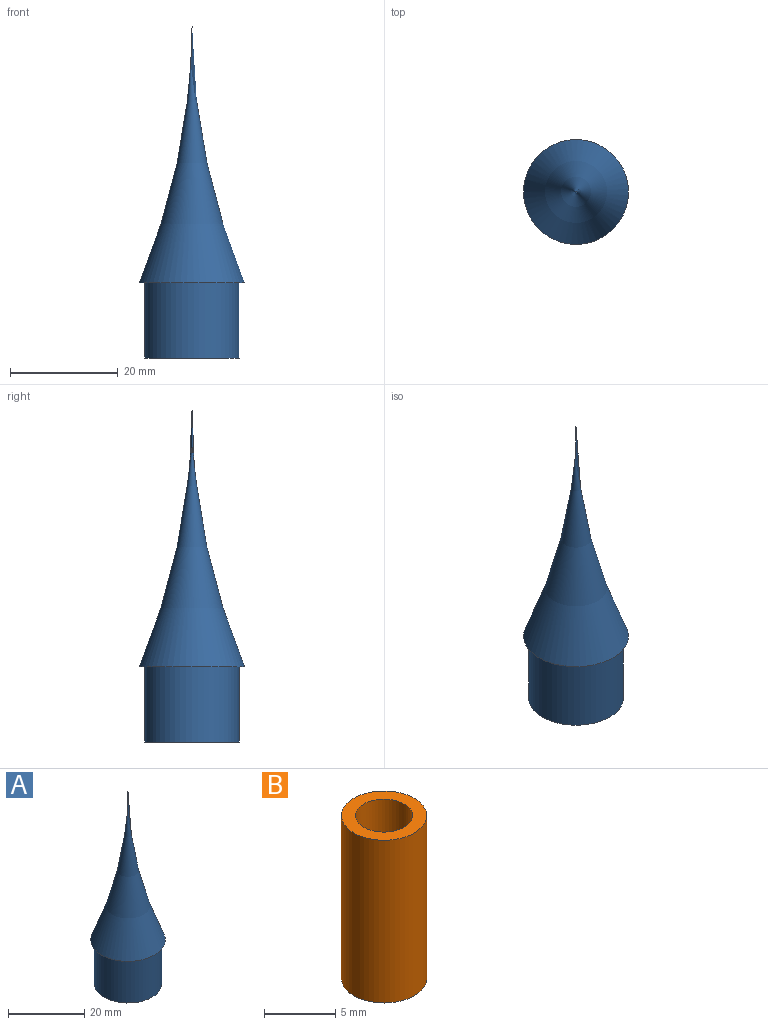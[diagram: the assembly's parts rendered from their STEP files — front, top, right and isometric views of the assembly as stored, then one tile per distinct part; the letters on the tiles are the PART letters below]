
ASSEMBLY  parts=2 mates=1
PART A: 7 faces, bbox 19.5x19.5x61.7 mm
  f0: plane 16.5x16.5mm, normal (0,0,1), area 22.7mm2, adj f1,f6
  f1: cylinder r=7.8mm len=15.6mm, axis (0,0,-1), area 735.1mm2, adj f0,f2
  f2: plane 17.6x17.6mm, normal (0,0,-1), area 52.2mm2, adj f1,f3
  f3: cylinder r=8.8mm len=17.6mm, axis (0,0,-1), area 774.1mm2, adj f2,f4
  f4: plane 19.49x19.49mm, normal (0,0,-1), area 55mm2, adj f3,f5
  f5: torus R=125.24mm, axis (0,0,-1), area 1019.9mm2, adj f4
  f6: torus R=125.24mm, axis (0,0,-1), area 707.7mm2, adj f0
PART B: 4 faces, bbox 6x6x14 mm
  f0: cylinder r=2mm len=14mm, axis (0,0,-1), area 175.9mm2, adj f2,f3
  f1: cylinder r=3mm len=14mm, axis (0,0,-1), area 263.9mm2, adj f2,f3
  f2: plane 6x6mm, normal (0,0,1), area 15.7mm2, adj f0,f1
  f3: plane 6x6mm, normal (0,0,-1), area 15.7mm2, adj f0,f1
PLACE A at identity
PLACE B t=(0,5.48,0)mm
MATE planar B.f1 <-> A.f1  axis (0,0,-1) through (0,5.48,0)mm
